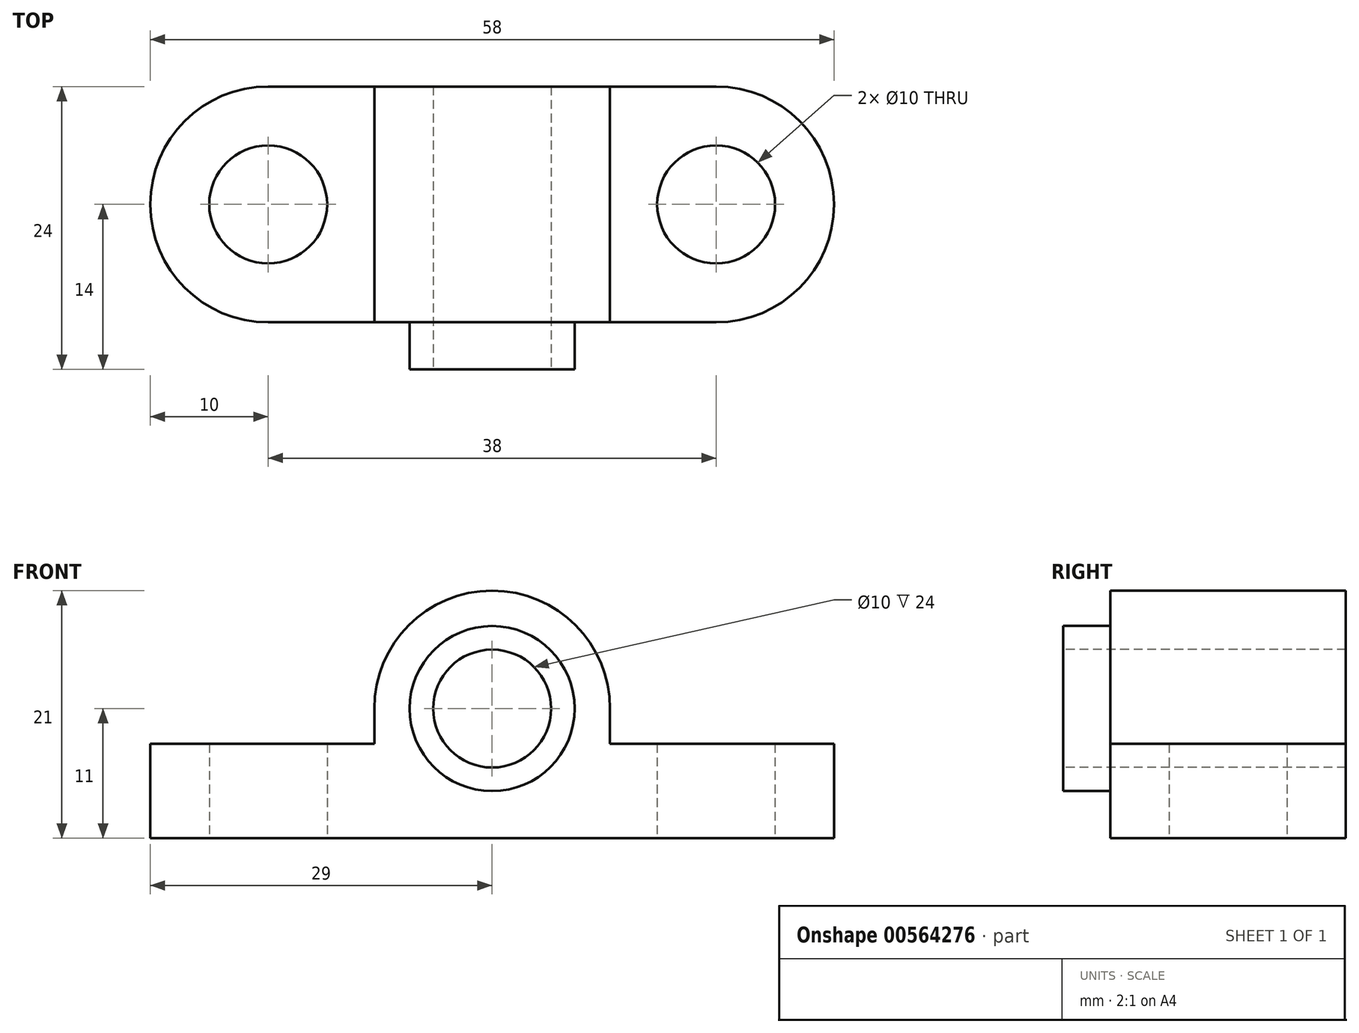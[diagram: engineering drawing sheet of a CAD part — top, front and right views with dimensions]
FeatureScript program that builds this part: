
annotation { "Feature Type Name" : "Feature", "Feature Type Description" : "" }
export const myFeature = defineFeature(function(context is Context, id is Id, definition is map)
    precondition{}
    {
        {
            var Q0;
            Q0=qCreatedBy(makeId("Top.planeOp"),FACE);
            var sketch = newSketch(context, id + "F0", { "sketchPlane" : qUnion([Q0])});
            skLineSegment(sketch, "E0.bottom", {"start": v(19, -10) * mm, "end": v(-19, -10) * mm});
            skLineSegment(sketch, "E0.top", {"start": v(19, 10) * mm, "end": v(-19, 10) * mm});
            skPoint(sketch, "E0.middle", {"position": v(0, 0) * mm});
            skArc(sketch, "E1", {"start": v(-19, 10) * mm, "mid": v(-29, 0) * mm, "end": v(-19, -10) * mm});
            skArc(sketch, "E2", {"start": v(19, -10) * mm, "mid": v(29, 0) * mm, "end": v(19, 10) * mm});
            skCircle(sketch, "E3", {"center": v(-19, 0) * mm, "radius": 5 * mm});
            skCircle(sketch, "E4", {"center": v(19, 0) * mm, "radius": 5 * mm});
            skSolve(sketch);
        }
        {
            var Q0;
            Q0=qSketchRegion(id+"F0",true);
            extrude(context, id + "F1", {"entities" : qUnion([Q0]), "depth" : 8 * mm, "offsetDistance" : 25 * mm});
        }
        {
            var Q0;
            Q0=makeQuery(id+"F1.opExtrude","SWEPT_FACE",FACE,{"disambiguationData":[OSD([sQuery(id+"F0.wireOp",EDGE,"E0.bottom")])]});
            var sketch = newSketch(context, id + "F2", { "sketchPlane" : qUnion([Q0])});
            skLineSegment(sketch, "E5", {"start": v(-10, 8) * mm, "end": v(-10, 11) * mm});
            skLineSegment(sketch, "E6", {"start": v(10, 8) * mm, "end": v(10, 11) * mm});
            skArc(sketch, "E7", {"start": v(10, 11) * mm, "mid": v(0, 21) * mm, "end": v(-10, 11) * mm});
            skCircle(sketch, "E8", {"center": v(0, 11) * mm, "radius": 7 * mm});
            skCircle(sketch, "E9", {"center": v(0, 11) * mm, "radius": 5 * mm});
            skSolve(sketch);
        }
        {
            var Q0;
            {var subQ5=sQuery(id+"F2.wireOp",EDGE,"E5");Q0=makeQuery(id+"F2.imprint","IMPRINT",FACE,{"disambiguationData":[TD([[makeQuery(id+"F2.imprint","IMPRINT",EDGE,{"derivedFrom":subQ5}),-1.0]])]});}
            var Q1;
            {var subQ0=sQuery(id+"F2.wireOp",EDGE,"E8");var subQ1=makeQuery(id+"F1.opExtrude","CAP_EDGE",EDGE,{"disambiguationData":[OSD([sQuery(id+"F0.wireOp",EDGE,"E0.bottom")])],"isStart":false});var subQ2=makeQuery(id+"F2.imprint","INTERSECT",VERTEX,{"disambiguationData":[OD(0.0)],"derivedFrom":[subQ1,subQ0]});Q1=makeQuery(id+"F2.imprint","IMPRINT",FACE,{"disambiguationData":[TD([[makeQuery(id+"F2.imprint","IMPRINT",EDGE,{"disambiguationData":[TD([[subQ2,1.0]])],"derivedFrom":subQ0}),1.0]])]});}
            var Q2;
            Q2=makeQuery(id+"F1.opExtrude","SWEPT_FACE",FACE,{"disambiguationData":[OSD([sQuery(id+"F0.wireOp",EDGE,"E0.top")])]});
            extrude(context, id + "F3", {"entities" : qUnion([Q0, Q1]), "operationType" : NewBodyOperationType.ADD, "endBound" : BoundingType.UP_TO_SURFACE, "oppositeDirection" : true, "endBoundEntityFace" : qUnion([Q2]), "depth" : 25 * mm});
        }
        {
            var Q0;
            {var subQ0=sQuery(id+"F2.wireOp",EDGE,"E9");var subQ1=makeQuery(id+"F1.opExtrude","CAP_EDGE",EDGE,{"disambiguationData":[OSD([sQuery(id+"F0.wireOp",EDGE,"E0.bottom")])],"isStart":false});var subQ2=makeQuery(id+"F2.imprint","INTERSECT",VERTEX,{"disambiguationData":[OD(0.0)],"derivedFrom":[subQ1,subQ0]});Q0=makeQuery(id+"F2.imprint","IMPRINT",FACE,{"disambiguationData":[TD([[makeQuery(id+"F2.imprint","IMPRINT",EDGE,{"disambiguationData":[TD([[subQ2,-1.0]])],"derivedFrom":subQ0}),1.0]])]});}
            extrude(context, id + "F4", {"entities" : qUnion([Q0]), "operationType" : NewBodyOperationType.REMOVE, "endBound" : BoundingType.THROUGH_ALL, "oppositeDirection" : true, "depth" : 25 * mm});
        }
        {
            var Q0;
            {var subQ0=sQuery(id+"F2.wireOp",EDGE,"E8");var subQ1=makeQuery(id+"F1.opExtrude","CAP_EDGE",EDGE,{"disambiguationData":[OSD([sQuery(id+"F0.wireOp",EDGE,"E0.bottom")])],"isStart":false});var subQ2=makeQuery(id+"F2.imprint","INTERSECT",VERTEX,{"disambiguationData":[OD(0.0)],"derivedFrom":[subQ1,subQ0]});Q0=makeQuery(id+"F2.imprint","IMPRINT",FACE,{"disambiguationData":[TD([[makeQuery(id+"F2.imprint","IMPRINT",EDGE,{"disambiguationData":[TD([[subQ2,1.0]])],"derivedFrom":subQ0}),1.0]])]});}
            var Q1;
            {var subQ0=sQuery(id+"F2.wireOp",EDGE,"E8");var subQ1=makeQuery(id+"F1.opExtrude","CAP_EDGE",EDGE,{"disambiguationData":[OSD([sQuery(id+"F0.wireOp",EDGE,"E0.bottom")])],"isStart":false});var subQ2=makeQuery(id+"F2.imprint","INTERSECT",VERTEX,{"disambiguationData":[OD(0.0)],"derivedFrom":[subQ1,subQ0]});Q1=makeQuery(id+"F2.imprint","IMPRINT",FACE,{"disambiguationData":[TD([[makeQuery(id+"F2.imprint","IMPRINT",EDGE,{"disambiguationData":[TD([[subQ2,-1.0]])],"derivedFrom":subQ0}),1.0]])]});}
            extrude(context, id + "F5", {"entities" : qUnion([Q0, Q1]), "operationType" : NewBodyOperationType.ADD, "depth" : 4 * mm});
        }
    });
